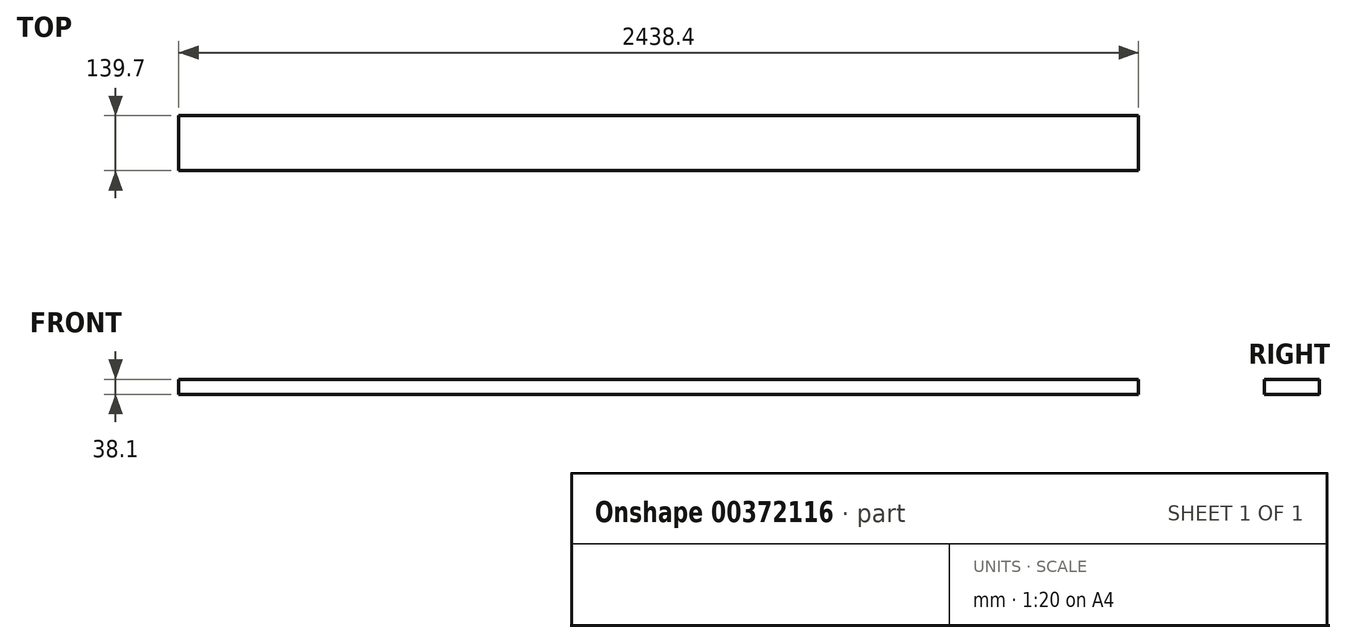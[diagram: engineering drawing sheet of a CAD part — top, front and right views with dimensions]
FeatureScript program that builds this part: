
annotation { "Feature Type Name" : "Feature", "Feature Type Description" : "" }
export const myFeature = defineFeature(function(context is Context, id is Id, definition is map)
    precondition{}
    {
        {
            var Q0;
            Q0=qCreatedBy(makeId("Top.planeOp"),FACE);
            var sketch = newSketch(context, id + "F0", { "sketchPlane" : qUnion([Q0])});
            skLineSegment(sketch, "E0.bottom", {"start": v(1219.2, -69.85) * mm, "end": v(-1219.2, -69.85) * mm});
            skLineSegment(sketch, "E0.top", {"start": v(1219.2, 69.85) * mm, "end": v(-1219.2, 69.85) * mm});
            skLineSegment(sketch, "E0.left", {"start": v(1219.2, -69.85) * mm, "end": v(1219.2, 69.85) * mm});
            skLineSegment(sketch, "E0.right", {"start": v(-1219.2, -69.85) * mm, "end": v(-1219.2, 69.85) * mm});
            skPoint(sketch, "E0.middle", {"position": v(0, 0) * mm});
            skSolve(sketch);
        }
        {
            var Q0;
            Q0=qSketchRegion(id+"F0",true);
            extrude(context, id + "F1", {"entities" : qUnion([Q0]), "oppositeDirection" : true, "depth" : 38.1 * mm});
        }
    });
